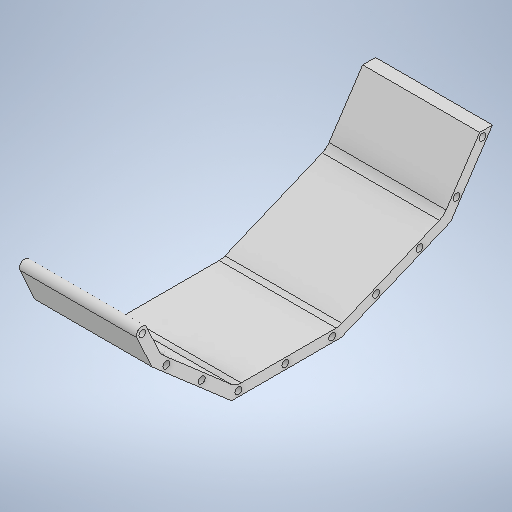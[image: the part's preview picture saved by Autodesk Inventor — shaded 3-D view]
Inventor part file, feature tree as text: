
AUTODESK INVENTOR PART (.ipt)
format: ipt  version: 2025.2 (Build 292293000, 293)  size: 962,048 bytes
history: native  units: mm
features: projected_geometry x13, extrude x11, sketch x11, chamfer x3, pattern_linear x3, other x3, fillet x1, reference x1
ambient origin geometry x8: Origin, YZ Plane, XZ Plane, XY Plane, X Axis, Y Axis, Z Axis, Center Point
bodies: Solid1 (feature_tree)
feature tree (46):
  extrude  "Extrusion1"  Depth=180.0mm
  extrude  "Extrusion16"  Depth=90.0mm
  extrude  "Extrusion17"  Depth=117.0mm
  chamfer  "Chamfer1"  Distance=77.4mm
  chamfer  "Chamfer2"  [1 undecoded]
  chamfer  "Chamfer3"  [1 undecoded]
  extrude  "Extrusion18"  Depth=20.0mm TaperAngle=45.0deg
  extrude  "Extrusion19"  TaperAngle=0.0deg  [1 undecoded]
  sketch  "Sketch19"  dims[d10=50.0mm]
  extrude  "Extrusion20"  Depth=7.05mm
  sketch  "Sketch20"  dims[d11=45.0deg]
  pattern_linear  "Rectangular Pattern7"  Spacing1=0.0mm  [1 undecoded]
  extrude  "Extrusion22"  Depth=3.525mm
  pattern_linear  "Rectangular Pattern8"  Spacing1=3.525mm  [1 undecoded]
  extrude  "Extrusion23"  Depth=3.525mm
  pattern_linear  "Rectangular Pattern9"  Spacing1=0.0mm  [1 undecoded]
  extrude  "Extrusion24"  Depth=7.05mm
  extrude  "Extrusion25"  Depth=7.05mm
  fillet  "Fillet4"  Radius=3.525mm
  extrude  "Extrusion26"  Depth=3.0mm
  sketch  "Sketch1"  dims[d0=100.0mm d1=180.0mm]
  sketch  "Sketch15"  dims[d2=90.0mm d3=76.5mm]
  projected_geometry  "Projected Loop7"
  sketch  "Sketch16"  dims[d4=7.15585mm d5=117.0mm]
  sketch  "Sketch17"  dims[d7=7.15585mm]
  projected_geometry  "Projected Loop8"
  sketch  "Sketch18"  dims[d9=30.0mm]
  sketch  "Sketch21"  dims[d12=38.0mm d13=77.4mm d14=0.0mm d79=0.0mm d80=0.0mm]
  sketch  "Sketch22"  dims[d81=31.5mm d82=0.0mm d83=0.0mm]
  sketch  "Sketch23"  dims[d84=30.0mm d85=2.0mm d86=45.0deg d87=20.0mm d88=2.0mm d89=45.0deg]
  reference  "Reference1"
  projected_geometry  "Projected Loop9"
  sketch  "Sketch24"  dims[d90=10.0mm d91=2.0mm d92=45.0deg d93=0.0mm d94=0.0mm d95=7.05mm d96=0.0mm d97=0.0mm d98=3.525mm d99=3.525mm d100=3.525mm d104=0.0mm d105=0.0mm d109=7.05mm d110=7.05mm d111=3.525mm d114=3.0mm d115=3.0mm d118=4.45mm d124=100.0mm d126=8.0mm d127=0.0mm d128=100.0mm d130=8.0mm d131=0.0mm d132=100.0mm d134=0.0mm d135=0.0mm d136=10.0mm d137=0.0mm d138=10.0mm d139=0.2mm d140=0.0mm]
  projected_geometry  "Projected Loop10"
  projected_geometry  "Projected Loop11"
  projected_geometry  "Projected Loop12"
  projected_geometry  "Projected Loop13"
  projected_geometry  "Projected Loop14"
  projected_geometry  "Projected Loop15"
  projected_geometry  "Projected Loop16"
  projected_geometry  "Projected Loop17"
  projected_geometry  "Projected Loop18"
  projected_geometry  "Projected Loop19"
  parser-record x1  (decoder bookkeeping rows leaked as tree rows — omitted from the tree; the rows remain in map.json)
  other  "WBR.iam"
  other  "inner_body_c:1"
note: 6 required parameter values undecoded (feature->parameter linkage not recoverable at this tier; creation-order binding heuristic only, values carry confidence <= 0.55)
note: 1 file-system path scrubbed to <path> (originals preserved in map.json)
